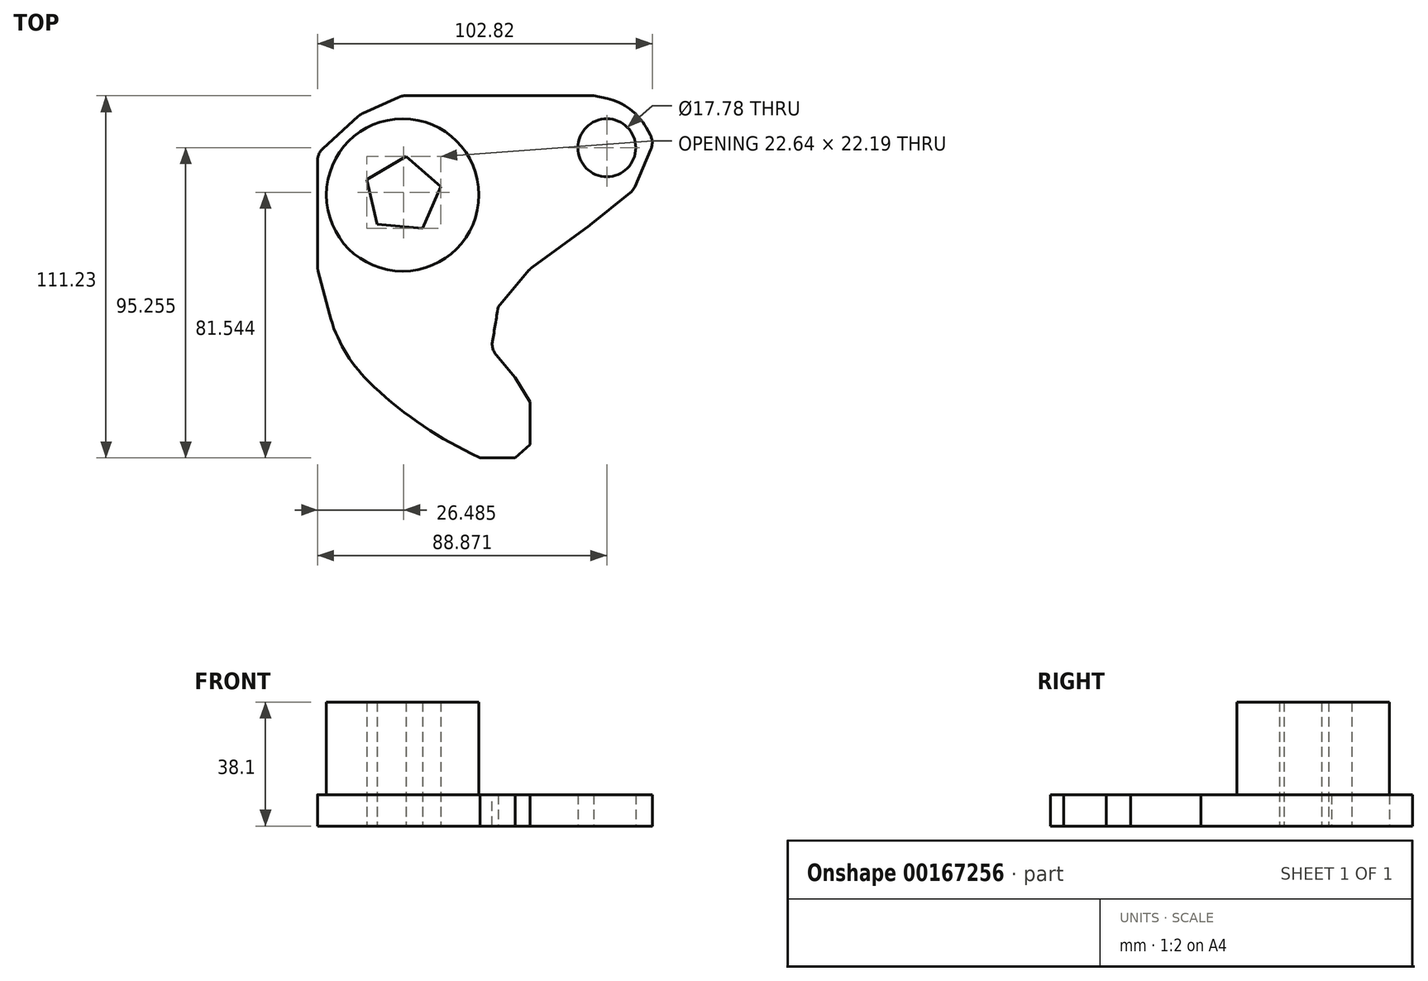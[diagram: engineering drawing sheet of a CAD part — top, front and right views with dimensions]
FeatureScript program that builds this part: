
annotation { "Feature Type Name" : "Feature", "Feature Type Description" : "" }
export const myFeature = defineFeature(function(context is Context, id is Id, definition is map)
    precondition{}
    {
        {
            var Q0;
            Q0=qCreatedBy(makeId("Top.planeOp"),FACE);
            var sketch = newSketch(context, id + "F0", { "sketchPlane" : qUnion([Q0])});
            skCircle(sketch, "E0", {"center": v(-27, 34.41) * mm, "radius": 23.41 * mm});
            skCircle(sketch, "E1", {"center": v(35.72, 48.94) * mm, "radius": 8.32 * mm});
            skLineSegment(sketch, "E2", {"start": v(-18.3, -14.96) * mm, "end": v(-11.9, -14.96) * mm});
            skLineSegment(sketch, "E3", {"start": v(-11.9, -14.96) * mm, "end": v(5.8, -32.1) * mm});
            skLineSegment(sketch, "E4", {"start": v(5.8, -32.1) * mm, "end": v(5.8, -40.22) * mm});
            skLineSegment(sketch, "E5", {"start": v(5.8, -40.22) * mm, "end": v(5.8, -43.42) * mm});
            skLineSegment(sketch, "E6", {"start": v(-18.3, -14.96) * mm, "end": v(-18.3, -17.28) * mm});
            skLineSegment(sketch, "E7", {"start": v(-18.3, -17.28) * mm, "end": v(-18.3, -20.47) * mm});
            skLineSegment(sketch, "E8", {"start": v(-18.3, -20.47) * mm, "end": v(-11.04, -28.6) * mm});
            skLineSegment(sketch, "E9", {"start": v(-11.04, -28.6) * mm, "end": v(0, -40.22) * mm});
            skLineSegment(sketch, "E10", {"start": v(0, -40.22) * mm, "end": v(5.8, -40.22) * mm});
            skCircle(sketch, "E11.cCircle", {"center": v(-27, 34.41) * mm, "radius": 9.67 * mm, "construction": true});
            skLineSegment(sketch, "E11.0", {"start": v(-25.9, 46.32) * mm, "end": v(-15.34, 37.03) * mm});
            skLineSegment(sketch, "E11.1", {"start": v(-15.34, 37.03) * mm, "end": v(-20.91, 24.13) * mm});
            skLineSegment(sketch, "E11.2", {"start": v(-20.91, 24.13) * mm, "end": v(-34.9, 25.44) * mm});
            skLineSegment(sketch, "E11.3", {"start": v(-34.9, 25.44) * mm, "end": v(-37.98, 39.15) * mm});
            skLineSegment(sketch, "E11.4", {"start": v(-37.98, 39.15) * mm, "end": v(-25.9, 46.32) * mm});
            skPoint(sketch, "E11.0.midPoint", {"position": v(-20.62, 41.67) * mm});
            skSolve(sketch);
        }
        {
            var Q0;
            Q0=qCreatedBy(makeId("Top.planeOp"),FACE);
            var sketch = newSketch(context, id + "F1", { "sketchPlane" : qUnion([Q0])});
            skLineSegment(sketch, "E12", {"start": v(-53.15, 31.51) * mm, "end": v(-53.15, 11.76) * mm});
            skLineSegment(sketch, "E13", {"start": v(-53.15, 11.76) * mm, "end": v(-46.76, -12.63) * mm});
            skLineSegment(sketch, "E14", {"start": v(-46.76, -12.63) * mm, "end": v(-34.56, -29.19) * mm});
            skLineSegment(sketch, "E15", {"start": v(-34.56, -29.19) * mm, "end": v(-18.3, -39.06) * mm});
            skLineSegment(sketch, "E16", {"start": v(-18.3, -39.06) * mm, "end": v(-3.2, -46.32) * mm});
            skLineSegment(sketch, "E17", {"start": v(-3.2, -46.32) * mm, "end": v(7.55, -46.32) * mm});
            skLineSegment(sketch, "E18", {"start": v(7.55, -46.32) * mm, "end": v(12.2, -42.26) * mm});
            skLineSegment(sketch, "E19", {"start": v(12.2, -42.26) * mm, "end": v(12.2, -36.16) * mm});
            skLineSegment(sketch, "E20", {"start": v(12.2, -36.16) * mm, "end": v(12.2, -29.19) * mm});
            skLineSegment(sketch, "E21", {"start": v(12.2, -29.19) * mm, "end": v(7.55, -21.64) * mm});
            skLineSegment(sketch, "E22", {"start": v(7.55, -21.64) * mm, "end": v(0, -12.63) * mm});
            skLineSegment(sketch, "E23", {"start": v(0, -12.63) * mm, "end": v(2.32, -3.92) * mm});
            skLineSegment(sketch, "E24", {"start": v(2.32, -3.92) * mm, "end": v(2.32, 0) * mm});
            skLineSegment(sketch, "E25", {"start": v(2.32, 0) * mm, "end": v(12.2, 11.76) * mm});
            skLineSegment(sketch, "E26", {"start": v(12.2, 11.76) * mm, "end": v(30.5, 25.12) * mm});
            skLineSegment(sketch, "E27", {"start": v(30.5, 25.12) * mm, "end": v(43.85, 35.87) * mm});
            skLineSegment(sketch, "E28", {"start": v(43.85, 35.87) * mm, "end": v(50.24, 50.68) * mm});
            skLineSegment(sketch, "E29", {"start": v(50.24, 50.68) * mm, "end": v(43.85, 62.3) * mm});
            skLineSegment(sketch, "E30", {"start": v(43.85, 62.3) * mm, "end": v(31.66, 64.9) * mm});
            skLineSegment(sketch, "E31", {"start": v(31.66, 64.9) * mm, "end": v(23.23, 64.9) * mm});
            skLineSegment(sketch, "E32", {"start": v(23.23, 64.9) * mm, "end": v(-27.3, 64.9) * mm});
            skLineSegment(sketch, "E33", {"start": v(-27.3, 64.9) * mm, "end": v(-40.08, 59.1) * mm});
            skLineSegment(sketch, "E34", {"start": v(-40.08, 59.1) * mm, "end": v(-53.15, 47.2) * mm});
            skLineSegment(sketch, "E35", {"start": v(-53.15, 47.2) * mm, "end": v(-53.15, 31.51) * mm});
            skSolve(sketch);
        }
        {
            var Q0;
            Q0 = qSketchRegion(id + "F1", true);
            extrude(context, id + "F2", {"entities" : qUnion([Q0]), "depth" : 9.65 * mm});
        }
        {
            var Q0;
            Q0=sQuery(id+"F0.wireOp",VERTEX,"E1.center");
            var Q1;
            Q1=makeQuery(id+"F2.opExtrude","SWEPT_BODY",BODY,{"disambiguationData":[OSD([sQuery(id+"F1.wireOp",EDGE,"E12"),sQuery(id+"F1.wireOp",EDGE,"E13"),sQuery(id+"F1.wireOp",EDGE,"E14"),sQuery(id+"F1.wireOp",EDGE,"E15"),sQuery(id+"F1.wireOp",EDGE,"E16"),sQuery(id+"F1.wireOp",EDGE,"E17"),sQuery(id+"F1.wireOp",EDGE,"E18"),sQuery(id+"F1.wireOp",EDGE,"E19"),sQuery(id+"F1.wireOp",EDGE,"E20"),sQuery(id+"F1.wireOp",EDGE,"E21"),sQuery(id+"F1.wireOp",EDGE,"E22"),sQuery(id+"F1.wireOp",EDGE,"E23"),sQuery(id+"F1.wireOp",EDGE,"E24"),sQuery(id+"F1.wireOp",EDGE,"E25"),sQuery(id+"F1.wireOp",EDGE,"E26"),sQuery(id+"F1.wireOp",EDGE,"E27"),sQuery(id+"F1.wireOp",EDGE,"E28"),sQuery(id+"F1.wireOp",EDGE,"E29"),sQuery(id+"F1.wireOp",EDGE,"E30"),sQuery(id+"F1.wireOp",EDGE,"E31"),sQuery(id+"F1.wireOp",EDGE,"E32"),sQuery(id+"F1.wireOp",EDGE,"E33"),sQuery(id+"F1.wireOp",EDGE,"E34"),sQuery(id+"F1.wireOp",EDGE,"E35")])]});
            hole(context, id + "F3", {"style" : HoleStyle.SIMPLE, "endStyle" : HoleEndStyle.THROUGH, "oppositeDirection" : true, "holeDiameter" : 17.78 * mm, "locations" : qUnion([Q0]), "scope" : qUnion([Q1]), "isTappedThrough" : true});
        }
        {
            var Q0;
            Q0=makeQuery(id+"F2.opExtrude","SWEPT_EDGE",EDGE,{"disambiguationData":[OSD([sQuery(id+"F1.wireOp",EDGE,"E28"),sQuery(id+"F1.wireOp",EDGE,"E29")])]});
            var Q1;
            Q1=makeQuery(id+"F2.opExtrude","SWEPT_EDGE",EDGE,{"disambiguationData":[OSD([sQuery(id+"F1.wireOp",EDGE,"E27"),sQuery(id+"F1.wireOp",EDGE,"E28")])]});
            var Q2;
            Q2=makeQuery(id+"F2.opExtrude","SWEPT_EDGE",EDGE,{"disambiguationData":[OSD([sQuery(id+"F1.wireOp",EDGE,"E26"),sQuery(id+"F1.wireOp",EDGE,"E27")])]});
            var Q3;
            Q3=makeQuery(id+"F2.opExtrude","SWEPT_EDGE",EDGE,{"disambiguationData":[OSD([sQuery(id+"F1.wireOp",EDGE,"E25"),sQuery(id+"F1.wireOp",EDGE,"E26")])]});
            var Q4;
            Q4=makeQuery(id+"F2.opExtrude","SWEPT_EDGE",EDGE,{"disambiguationData":[OSD([sQuery(id+"F1.wireOp",EDGE,"E22"),sQuery(id+"F1.wireOp",EDGE,"E23")])]});
            fillet(context, id + "F4", {"entities" : qUnion([Q0, Q1, Q2, Q3, Q4]), "radius" : 5.08 * mm, "tangentPropagation" : true, "allowEdgeOverflow" : false});
        }
        {
            var Q0;
            Q0=makeQuery(id+"F2.opExtrude","SWEPT_EDGE",EDGE,{"disambiguationData":[OSD([sQuery(id+"F1.wireOp",EDGE,"E12"),sQuery(id+"F1.wireOp",EDGE,"E13")])]});
            var Q1;
            Q1=makeQuery(id+"F2.opExtrude","SWEPT_EDGE",EDGE,{"disambiguationData":[OSD([sQuery(id+"F1.wireOp",EDGE,"E34"),sQuery(id+"F1.wireOp",EDGE,"E35")])]});
            var Q2;
            Q2=makeQuery(id+"F2.opExtrude","SWEPT_EDGE",EDGE,{"disambiguationData":[OSD([sQuery(id+"F1.wireOp",EDGE,"E33"),sQuery(id+"F1.wireOp",EDGE,"E34")])]});
            var Q3;
            Q3=makeQuery(id+"F2.opExtrude","SWEPT_EDGE",EDGE,{"disambiguationData":[OSD([sQuery(id+"F1.wireOp",EDGE,"E32"),sQuery(id+"F1.wireOp",EDGE,"E33")])]});
            fillet(context, id + "F5", {"entities" : qUnion([Q0, Q1, Q2, Q3]), "radius" : 5.08 * mm, "tangentPropagation" : true, "allowEdgeOverflow" : false});
        }
        {
            var Q0;
            Q0=sQuery(id+"F0.wireOp",VERTEX,"E0.center");
            var Q1;
            Q1=makeQuery(id+"F2.opExtrude","SWEPT_BODY",BODY,{"disambiguationData":[OSD([sQuery(id+"F1.wireOp",EDGE,"E12"),sQuery(id+"F1.wireOp",EDGE,"E13"),sQuery(id+"F1.wireOp",EDGE,"E14"),sQuery(id+"F1.wireOp",EDGE,"E15"),sQuery(id+"F1.wireOp",EDGE,"E16"),sQuery(id+"F1.wireOp",EDGE,"E17"),sQuery(id+"F1.wireOp",EDGE,"E18"),sQuery(id+"F1.wireOp",EDGE,"E19"),sQuery(id+"F1.wireOp",EDGE,"E20"),sQuery(id+"F1.wireOp",EDGE,"E21"),sQuery(id+"F1.wireOp",EDGE,"E22"),sQuery(id+"F1.wireOp",EDGE,"E23"),sQuery(id+"F1.wireOp",EDGE,"E24"),sQuery(id+"F1.wireOp",EDGE,"E25"),sQuery(id+"F1.wireOp",EDGE,"E26"),sQuery(id+"F1.wireOp",EDGE,"E27"),sQuery(id+"F1.wireOp",EDGE,"E28"),sQuery(id+"F1.wireOp",EDGE,"E29"),sQuery(id+"F1.wireOp",EDGE,"E30"),sQuery(id+"F1.wireOp",EDGE,"E31"),sQuery(id+"F1.wireOp",EDGE,"E32"),sQuery(id+"F1.wireOp",EDGE,"E33"),sQuery(id+"F1.wireOp",EDGE,"E34"),sQuery(id+"F1.wireOp",EDGE,"E35")])]});
            hole(context, id + "F6", {"style" : HoleStyle.SIMPLE, "endStyle" : HoleEndStyle.THROUGH, "oppositeDirection" : true, "holeDiameter" : 43.18 * mm, "locations" : qUnion([Q0]), "scope" : qUnion([Q1]), "isTappedThrough" : true});
        }
        {
            var Q0;
            Q0=makeQuery(id+"F0.imprint","IMPRINT",FACE,{"disambiguationData":[TD([[makeQuery(id+"F0.imprint","IMPRINT",EDGE,{"derivedFrom":sQuery(id+"F0.wireOp",EDGE,"E0")}),1.0]])]});
            extrude(context, id + "F7", {"entities" : qUnion([Q0]), "operationType" : NewBodyOperationType.ADD, "depth" : 38.1 * mm});
        }
        {
            var Q0;
            Q0=makeQuery(id+"F2.opExtrude","SWEPT_EDGE",EDGE,{"disambiguationData":[OSD([sQuery(id+"F1.wireOp",EDGE,"E14"),sQuery(id+"F1.wireOp",EDGE,"E15")])]});
            fillet(context, id + "F8", {"entities" : qUnion([Q0]), "radius" : 118.26 * mm, "tangentPropagation" : true, "allowEdgeOverflow" : false});
        }
        {
            var Q0;
            Q0=makeQuery(id+"F8.opFillet","BLEND_EDGE",EDGE,{"blendedFrom":[makeQuery(id+"F2.opExtrude","SWEPT_EDGE",EDGE,{"disambiguationData":[OSD([sQuery(id+"F1.wireOp",EDGE,"E14"),sQuery(id+"F1.wireOp",EDGE,"E15")])]}),makeQuery(id+"F2.opExtrude","SWEPT_FACE",FACE,{"disambiguationData":[OSD([sQuery(id+"F1.wireOp",EDGE,"E13")])]})],"blendedInto":[makeQuery(id+"F2.opExtrude","SWEPT_FACE",FACE,{"disambiguationData":[OSD([sQuery(id+"F1.wireOp",EDGE,"E13")])]})]});
            fillet(context, id + "F9", {"entities" : qUnion([Q0]), "radius" : 44.77 * mm, "tangentPropagation" : true, "allowEdgeOverflow" : false});
        }
        {
            var Q0;
            {var subQ0=sQuery(id+"F1.wireOp",EDGE,"E13");Q0=makeQuery(id+"F5.opFillet","BLEND_EDGE",EDGE,{"blendedFrom":[makeQuery(id+"F2.opExtrude","SWEPT_EDGE",EDGE,{"disambiguationData":[OSD([sQuery(id+"F1.wireOp",EDGE,"E12"),subQ0])]}),makeQuery(id+"F2.opExtrude","SWEPT_FACE",FACE,{"disambiguationData":[OSD([subQ0])]})],"blendedInto":[makeQuery(id+"F2.opExtrude","SWEPT_FACE",FACE,{"disambiguationData":[OSD([subQ0])]})]});}
            var Q1;
            Q1=makeQuery(id+"F2.opExtrude","SWEPT_EDGE",EDGE,{"disambiguationData":[OSD([sQuery(id+"F1.wireOp",EDGE,"E23"),sQuery(id+"F1.wireOp",EDGE,"E24")])]});
            fillet(context, id + "F10", {"entities" : qUnion([Q0, Q1]), "radius" : 683.3 * mm, "tangentPropagation" : true, "allowEdgeOverflow" : false});
        }
        {
            var Q0;
            Q0=makeQuery(id+"F2.opExtrude","SWEPT_EDGE",EDGE,{"disambiguationData":[OSD([sQuery(id+"F1.wireOp",EDGE,"E29"),sQuery(id+"F1.wireOp",EDGE,"E30")])]});
            fillet(context, id + "F11", {"entities" : qUnion([Q0]), "radius" : 17.9 * mm, "tangentPropagation" : true, "allowEdgeOverflow" : false});
        }
    });
